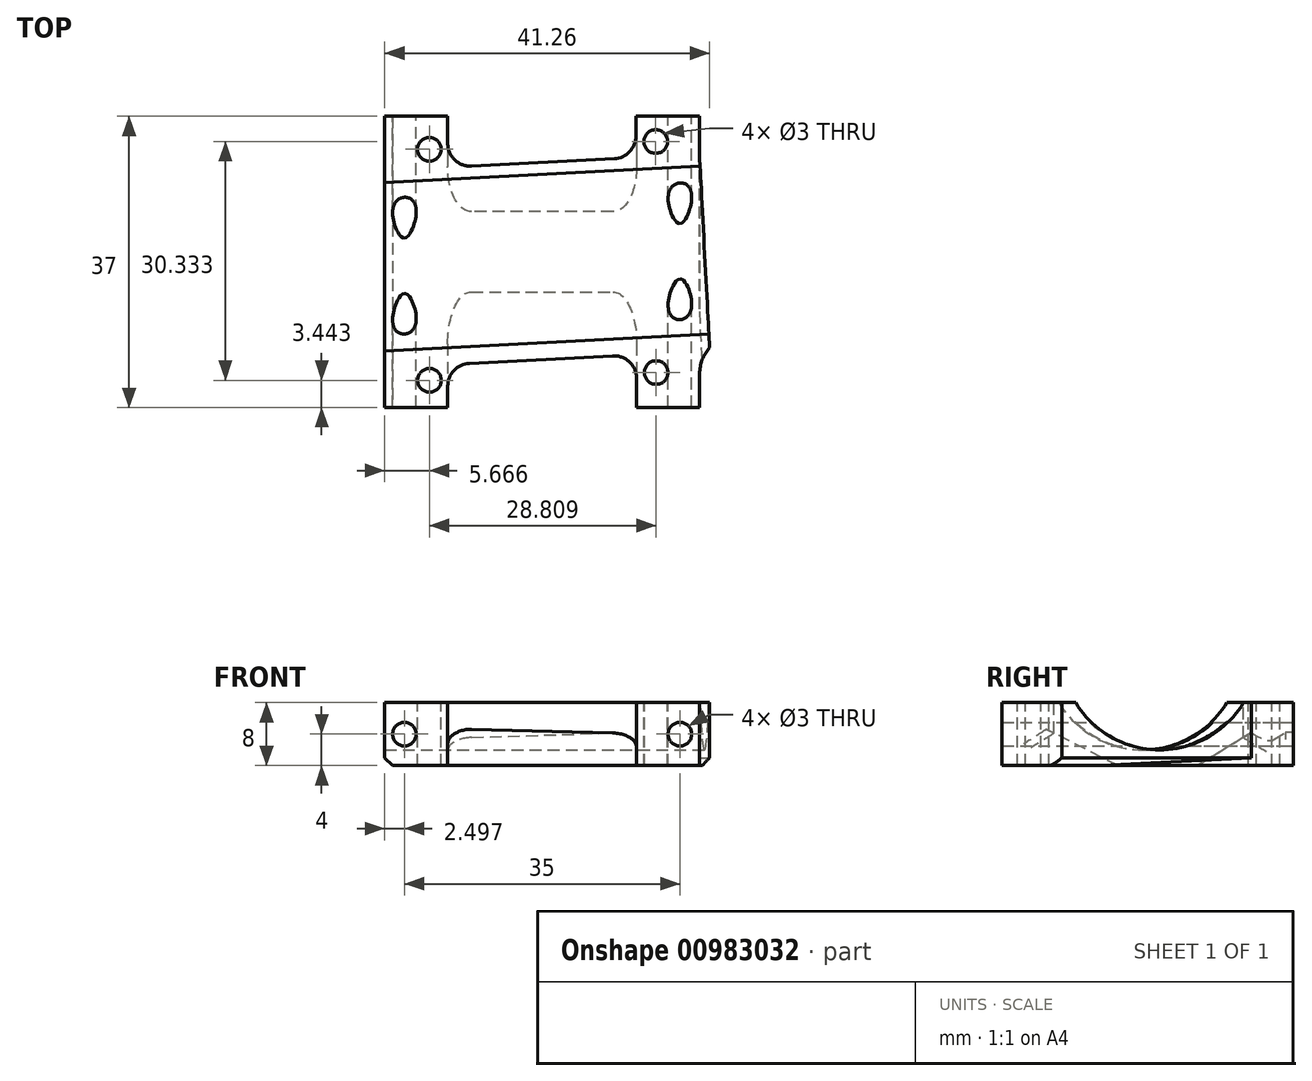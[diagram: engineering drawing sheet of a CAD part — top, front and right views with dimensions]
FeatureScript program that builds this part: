
annotation { "Feature Type Name" : "Feature", "Feature Type Description" : "" }
export const myFeature = defineFeature(function(context is Context, id is Id, definition is map)
    precondition{}
    {
        {
            var Q0;
            Q0=qCreatedBy(makeId("Top.planeOp"),FACE);
            var sketch = newSketch(context, id + "F0", { "sketchPlane" : qUnion([Q0])});
            skLineSegment(sketch, "E0.bottom", {"start": v(-25.77, 33.29) * mm, "end": v(14.23, 33.29) * mm});
            skLineSegment(sketch, "E0.top", {"start": v(-25.77, -1.71) * mm, "end": v(14.23, -1.71) * mm});
            skLineSegment(sketch, "E0.left", {"start": v(-25.77, 33.29) * mm, "end": v(-25.77, -1.71) * mm});
            skLineSegment(sketch, "E0.right", {"start": v(14.23, 33.29) * mm, "end": v(14.23, -1.71) * mm});
            skSolve(sketch);
        }
        {
            var Q0;
            Q0=qSketchRegion(id+"F0",true);
            extrude(context, id + "F1", {"entities" : qUnion([Q0]), "depth" : 8 * mm, "offsetDistance" : 25 * mm});
        }
        {
            var Q0;
            Q0=makeQuery(id+"F1.opExtrude","CAP_FACE",FACE,{"disambiguationData":[OSD([sQuery(id+"F0.wireOp",EDGE,"E0.bottom"),sQuery(id+"F0.wireOp",EDGE,"E0.top"),sQuery(id+"F0.wireOp",EDGE,"E0.left"),sQuery(id+"F0.wireOp",EDGE,"E0.right")])],"isStart":false});
            var sketch = newSketch(context, id + "F2", { "sketchPlane" : qUnion([Q0])});
            skLineSegment(sketch, "E1", {"start": v(-25.77, 28.93) * mm, "end": v(-27.03, 4.89) * mm});
            skLineSegment(sketch, "E2", {"start": v(-27.03, 4.89) * mm, "end": v(-25.77, 4.82) * mm});
            skLineSegment(sketch, "E3", {"start": v(-25.77, 4.82) * mm, "end": v(-23.4, 26.1) * mm});
            skLineSegment(sketch, "E4", {"start": v(-23.4, 26.1) * mm, "end": v(-25.77, 28.93) * mm});
            skSolve(sketch);
        }
        {
            var Q0;
            Q0=qSketchRegion(id+"F2",true);
            extrude(context, id + "F3", {"entities" : qUnion([Q0]), "operationType" : NewBodyOperationType.ADD, "oppositeDirection" : true, "depth" : 8 * mm, "offsetDistance" : 25 * mm});
        }
        {
            var Q0;
            Q0=makeQuery(id+"F3.opExtrude","SWEPT_FACE",FACE,{"disambiguationData":[OSD([sQuery(id+"F2.wireOp",EDGE,"E1")])]});
            var sketch = newSketch(context, id + "F4", { "sketchPlane" : qUnion([Q0])});
            skCircle(sketch, "E5", {"center": v(-15.9, 14.5) * mm, "radius": 12.5 * mm});
            skSolve(sketch);
        }
        {
            var Q0;
            Q0=qSketchRegion(id+"F4",true);
            extrude(context, id + "F5", {"entities" : qUnion([Q0]), "operationType" : NewBodyOperationType.REMOVE, "oppositeDirection" : true, "depth" : 64.1 * mm, "offsetDistance" : 25 * mm});
        }
        {
            var Q0;
            {var subQ1=sQuery(id+"F0.wireOp",EDGE,"E0.left");var subQ2=sQuery(id+"F0.wireOp",EDGE,"E0.right");var subQ3=sQuery(id+"F0.wireOp",EDGE,"E0.bottom");Q0=makeQuery(id+"F5.boolean.opBoolean","SPLIT",FACE,{"disambiguationData":[TD([makeQuery(id+"F1.opExtrude","SWEPT_FACE",FACE,{"disambiguationData":[OSD([subQ3])]})])],"derivedFrom":makeQuery(id+"F3.boolean.opBoolean","MERGE",FACE,{"derivedFrom":[makeQuery(id+"F1.opExtrude","CAP_FACE",FACE,{"disambiguationData":[OSD([subQ3,sQuery(id+"F0.wireOp",EDGE,"E0.top"),subQ1,subQ2])],"isStart":false}),makeQuery(id+"F3.opExtrude","CAP_FACE",FACE,{"disambiguationData":[OSD([sQuery(id+"F2.wireOp",EDGE,"E1"),sQuery(id+"F2.wireOp",EDGE,"E2"),sQuery(id+"F2.wireOp",EDGE,"E3"),sQuery(id+"F2.wireOp",EDGE,"E4")])],"isStart":true})]})});}
            var sketch = newSketch(context, id + "F6", { "sketchPlane" : qUnion([Q0])});
            skLineSegment(sketch, "E6", {"start": v(-14.93, 28.9) * mm, "end": v(3.18, 27.94) * mm});
            skLineSegment(sketch, "E7.0", {"start": v(-14.72, 3.85) * mm, "end": v(3.48, 2.9) * mm});
            skLineSegment(sketch, "E8.0", {"start": v(6.23, 0) * mm, "end": v(6.23, -1.71) * mm});
            skLineSegment(sketch, "E9.0", {"start": v(-17.77, 0.95) * mm, "end": v(-17.77, -1.71) * mm});
            skLineSegment(sketch, "E10.0", {"start": v(6.23, 33.29) * mm, "end": v(6.23, 30.84) * mm});
            skCircle(sketch, "E11", {"center": v(-20.25, 1.73) * mm, "radius": 1.5 * mm});
            skCircle(sketch, "E12", {"center": v(8.56, 30.09) * mm, "radius": 1.5 * mm});
            skCircle(sketch, "E13", {"center": v(-20.2, 31.07) * mm, "radius": 1.5 * mm});
            skLineSegment(sketch, "E14", {"start": v(-17.68, 31.79) * mm, "end": v(-17.68, 33.29) * mm});
            skPoint(sketch, "E15.visualSharp", {"position": v(-17.68, 29.04) * mm});
            skArc(sketch, "E15.filletArc", {"start": v(-17.68, 31.79) * mm, "mid": v(-16.88, 29.8) * mm, "end": v(-14.93, 28.9) * mm});
            skPoint(sketch, "E16.visualSharp", {"position": v(6.23, 27.78) * mm});
            skArc(sketch, "E16.filletArc", {"start": v(3.18, 27.94) * mm, "mid": v(5.32, 28.74) * mm, "end": v(6.23, 30.84) * mm});
            skPoint(sketch, "E17.visualSharp", {"position": v(6.23, 2.75) * mm});
            skArc(sketch, "E17.filletArc", {"start": v(6.23, 0) * mm, "mid": v(5.43, 2) * mm, "end": v(3.48, 2.9) * mm});
            skPoint(sketch, "E18.visualSharp", {"position": v(-17.77, 4) * mm});
            skArc(sketch, "E18.filletArc", {"start": v(-14.72, 3.85) * mm, "mid": v(-16.87, 3.05) * mm, "end": v(-17.77, 0.95) * mm});
            skLineSegment(sketch, "E19", {"start": v(-17.77, -1.71) * mm, "end": v(-10.84, -6.86) * mm});
            skLineSegment(sketch, "E20", {"start": v(-10.84, -6.86) * mm, "end": v(6.23, -1.71) * mm});
            skLineSegment(sketch, "E21", {"start": v(-17.68, 33.29) * mm, "end": v(-3.16, 37.2) * mm});
            skLineSegment(sketch, "E22", {"start": v(-3.16, 37.2) * mm, "end": v(6.23, 33.29) * mm});
            skCircle(sketch, "E23", {"center": v(8.55, 0.73) * mm, "radius": 1.5 * mm});
            skSolve(sketch);
        }
        {
            var Q0;
            Q0=qSketchRegion(id+"F6",true);
            extrude(context, id + "F7", {"entities" : qUnion([Q0]), "operationType" : NewBodyOperationType.REMOVE, "oppositeDirection" : true, "depth" : 25 * mm, "offsetDistance" : 25 * mm});
        }
        {
            var Q0;
            {var subQ5=sQuery(id+"F0.wireOp",EDGE,"E0.left");var subQ7=sQuery(id+"F0.wireOp",EDGE,"E0.bottom");Q0=makeQuery(id+"F7.boolean.opBoolean","SPLIT",FACE,{"disambiguationData":[TD([makeQuery(id+"F1.opExtrude","SWEPT_FACE",FACE,{"disambiguationData":[OSD([subQ5])]})])],"derivedFrom":makeQuery(id+"F1.opExtrude","SWEPT_FACE",FACE,{"disambiguationData":[OSD([subQ7])]})});}
            var sketch = newSketch(context, id + "F8", { "sketchPlane" : qUnion([Q0])});
            skCircle(sketch, "E24", {"center": v(-11.73, 4) * mm, "radius": 1.5 * mm});
            skCircle(sketch, "E25", {"center": v(23.27, 4) * mm, "radius": 1.5 * mm});
            skSolve(sketch);
        }
        {
            var Q0;
            Q0=qSketchRegion(id+"F8",true);
            extrude(context, id + "F9", {"entities" : qUnion([Q0]), "operationType" : NewBodyOperationType.REMOVE, "oppositeDirection" : true, "depth" : 46.6 * mm, "offsetDistance" : 25 * mm});
        }
        {
            var Q0;
            Q0=makeQuery(id+"F3.opExtrude","SWEPT_EDGE",EDGE,{"disambiguationData":[OSD([sQuery(id+"F0.wireOp",EDGE,"E0.left"),sQuery(id+"F2.wireOp",EDGE,"E2"),sQuery(id+"F2.wireOp",EDGE,"E3")])]});
            fillet(context, id + "F10", {"entities" : qUnion([Q0]), "radius" : 5 * mm, "tangentPropagation" : true, "allowEdgeOverflow" : false});
        }
        {
            var Q0;
            Q0=makeQuery(id+"F7.boolean.opBoolean","COPY",FACE,{"derivedFrom":makeQuery(id+"F7.opExtrude","SWEPT_FACE",FACE,{"disambiguationData":[OSD([sQuery(id+"F6.wireOp",EDGE,"E8.0")])]})});
            var sketch = newSketch(context, id + "F11", { "sketchPlane" : qUnion([Q0])});
            skLineSegment(sketch, "E26", {"start": v(-37.97, 9.77) * mm, "end": v(-21.04, -0.7) * mm});
            skLineSegment(sketch, "E27", {"start": v(-13.35, -0.7) * mm, "end": v(0, 6.1) * mm});
            skLineSegment(sketch, "E28", {"start": v(-37.97, 9.77) * mm, "end": v(-37.97, -11.82) * mm});
            skLineSegment(sketch, "E29", {"start": v(-37.97, -11.82) * mm, "end": v(-21.04, -0.7) * mm});
            skLineSegment(sketch, "E30", {"start": v(-13.35, -0.7) * mm, "end": v(-2.57, -3.45) * mm});
            skLineSegment(sketch, "E31", {"start": v(0, 6.1) * mm, "end": v(4.72, 8.5) * mm});
            skLineSegment(sketch, "E32", {"start": v(4.72, 8.5) * mm, "end": v(6.07, -10.58) * mm});
            skLineSegment(sketch, "E33", {"start": v(6.07, -10.58) * mm, "end": v(-2.57, -3.45) * mm});
            skSolve(sketch);
        }
        {
            var Q0;
            Q0=qSketchRegion(id+"F11",true);
            var Q1;
            Q1=makeQuery(id+"F7.boolean.opBoolean","COPY",FACE,{"derivedFrom":makeQuery(id+"F7.opExtrude","SWEPT_FACE",FACE,{"disambiguationData":[OSD([sQuery(id+"F6.wireOp",EDGE,"E9.0")])]})});
            extrude(context, id + "F12", {"entities" : qUnion([Q0]), "operationType" : NewBodyOperationType.REMOVE, "endBound" : BoundingType.UP_TO_SURFACE, "depth" : 25 * mm, "endBoundEntityFace" : qUnion([Q1]), "offsetDistance" : 25 * mm});
        }
        {
            var Q0;
            Q0=makeQuery(id+"F12.boolean.opBoolean","COPY",EDGE,{"derivedFrom":makeQuery(id+"F12.opExtrude","CAP_EDGE",EDGE,{"disambiguationData":[OSD([sQuery(id+"F11.wireOp",EDGE,"E26")])],"isStart":true})});
            var Q1;
            Q1=makeQuery(id+"F12.boolean.opBoolean","COPY",EDGE,{"derivedFrom":makeQuery(id+"F12.opExtrude","CAP_EDGE",EDGE,{"disambiguationData":[OSD([sQuery(id+"F11.wireOp",EDGE,"E27")])],"isStart":false})});
            var Q2;
            Q2=makeQuery(id+"F12.boolean.opBoolean","COPY",EDGE,{"derivedFrom":makeQuery(id+"F12.opExtrude","CAP_EDGE",EDGE,{"disambiguationData":[OSD([sQuery(id+"F11.wireOp",EDGE,"E26")])],"isStart":false})});
            var Q3;
            Q3=makeQuery(id+"F12.boolean.opBoolean","COPY",EDGE,{"derivedFrom":makeQuery(id+"F12.opExtrude","CAP_EDGE",EDGE,{"disambiguationData":[OSD([sQuery(id+"F11.wireOp",EDGE,"E27")])],"isStart":true})});
            fillet(context, id + "F13", {"entities" : qUnion([Q0, Q1, Q2, Q3]), "radius" : 3 * mm, "tangentPropagation" : true, "allowEdgeOverflow" : false});
        }
        {
            var Q0;
            Q0=makeQuery(id+"F1.opExtrude","CAP_EDGE",EDGE,{"disambiguationData":[OSD([sQuery(id+"F0.wireOp",EDGE,"E0.right")])],"isStart":true});
            var Q1;
            Q1=makeQuery(id+"F3.opExtrude","CAP_EDGE",EDGE,{"disambiguationData":[OSD([sQuery(id+"F2.wireOp",EDGE,"E1")])],"isStart":false});
            chamfer(context, id + "F14", {"entities" : qUnion([Q0, Q1]), "width" : 1 * mm, "tangentPropagation" : true});
        }
        {
            var Q0;
            {var subQ4=sQuery(id+"F0.wireOp",EDGE,"E0.right");var subQ6=sQuery(id+"F0.wireOp",EDGE,"E0.top");Q0=makeQuery(id+"F7.boolean.opBoolean","SPLIT",FACE,{"disambiguationData":[TD([makeQuery(id+"F1.opExtrude","SWEPT_FACE",FACE,{"disambiguationData":[OSD([subQ4])]})])],"derivedFrom":makeQuery(id+"F1.opExtrude","SWEPT_FACE",FACE,{"disambiguationData":[OSD([subQ6])]})});}
            var Q1;
            {var subQ5=sQuery(id+"F0.wireOp",EDGE,"E0.left");var subQ6=sQuery(id+"F0.wireOp",EDGE,"E0.top");Q1=makeQuery(id+"F7.boolean.opBoolean","SPLIT",FACE,{"disambiguationData":[TD([makeQuery(id+"F1.opExtrude","SWEPT_FACE",FACE,{"disambiguationData":[OSD([subQ5])]})])],"derivedFrom":makeQuery(id+"F1.opExtrude","SWEPT_FACE",FACE,{"disambiguationData":[OSD([subQ6])]})});}
            extrude(context, id + "F15", {"entities" : qUnion([Q0, Q1]), "operationType" : NewBodyOperationType.ADD, "depth" : 1 * mm, "offsetDistance" : 25 * mm});
        }
        {
            var Q0;
            {var subQ4=sQuery(id+"F0.wireOp",EDGE,"E0.right");var subQ7=sQuery(id+"F0.wireOp",EDGE,"E0.bottom");Q0=makeQuery(id+"F7.boolean.opBoolean","SPLIT",FACE,{"disambiguationData":[TD([makeQuery(id+"F1.opExtrude","SWEPT_FACE",FACE,{"disambiguationData":[OSD([subQ4])]})])],"derivedFrom":makeQuery(id+"F1.opExtrude","SWEPT_FACE",FACE,{"disambiguationData":[OSD([subQ7])]})});}
            var Q1;
            {var subQ5=sQuery(id+"F0.wireOp",EDGE,"E0.left");var subQ7=sQuery(id+"F0.wireOp",EDGE,"E0.bottom");Q1=makeQuery(id+"F7.boolean.opBoolean","SPLIT",FACE,{"disambiguationData":[TD([makeQuery(id+"F1.opExtrude","SWEPT_FACE",FACE,{"disambiguationData":[OSD([subQ5])]})])],"derivedFrom":makeQuery(id+"F1.opExtrude","SWEPT_FACE",FACE,{"disambiguationData":[OSD([subQ7])]})});}
            extrude(context, id + "F16", {"entities" : qUnion([Q0, Q1]), "operationType" : NewBodyOperationType.ADD, "depth" : 1 * mm, "offsetDistance" : 25 * mm});
        }
        {
            var Q0;
            Q0=makeQuery(id+"F1.opExtrude","SWEPT_BODY",BODY,{"disambiguationData":[OSD([sQuery(id+"F0.wireOp",EDGE,"E0.bottom"),sQuery(id+"F0.wireOp",EDGE,"E0.top"),sQuery(id+"F0.wireOp",EDGE,"E0.left"),sQuery(id+"F0.wireOp",EDGE,"E0.right")])]});
            var Q1;
            {var subQ0=sQuery(id+"F0.wireOp",EDGE,"E0.right");var subQ1=sQuery(id+"F0.wireOp",EDGE,"E0.bottom");var subQ2=sQuery(id+"F0.wireOp",EDGE,"E0.top");Q1=makeQuery(id+"F16.boolean.opBoolean","MERGE",FACE,{"derivedFrom":[makeQuery(id+"F15.boolean.opBoolean","MERGE",FACE,{"derivedFrom":[makeQuery(id+"F1.opExtrude","SWEPT_FACE",FACE,{"disambiguationData":[OSD([subQ0])]}),makeQuery(id+"F15.opExtrude","SWEPT_FACE",FACE,{"disambiguationData":[OSD([subQ2,subQ0]),TDD([makeQuery(id+"F1.opExtrude","SWEPT_EDGE",EDGE,{"disambiguationData":[OSD([subQ2,subQ0])]})])]})]}),makeQuery(id+"F16.opExtrude","SWEPT_FACE",FACE,{"disambiguationData":[OSD([subQ1,subQ0]),TDD([makeQuery(id+"F1.opExtrude","SWEPT_EDGE",EDGE,{"disambiguationData":[OSD([subQ1,subQ0])]})])]})]});}
            mirror(context, id + "F17", {"operationType" : NewBodyOperationType.ADD, "entities" : qUnion([Q0]), "mirrorPlane" : qUnion([Q1])});
        }
        {
            var Q0;
            {var subQ0=sQuery(id+"F2.wireOp",EDGE,"E1");var subQ1=makeQuery(id+"F3.opExtrude","CAP_FACE",FACE,{"disambiguationData":[OSD([subQ0,sQuery(id+"F2.wireOp",EDGE,"E2"),sQuery(id+"F2.wireOp",EDGE,"E3"),sQuery(id+"F2.wireOp",EDGE,"E4")])],"isStart":true});var subQ2=sQuery(id+"F0.wireOp",EDGE,"E0.right");var subQ3=sQuery(id+"F0.wireOp",EDGE,"E0.left");var subQ4=sQuery(id+"F0.wireOp",EDGE,"E0.bottom");var subQ5=makeQuery(id+"F1.opExtrude","CAP_FACE",FACE,{"disambiguationData":[OSD([subQ4,sQuery(id+"F0.wireOp",EDGE,"E0.top"),subQ3,subQ2])],"isStart":false});var subQ6=makeQuery(id+"F1.opExtrude","SWEPT_FACE",FACE,{"disambiguationData":[OSD([subQ2])]});var subQ7=makeQuery(id+"F1.opExtrude","SWEPT_FACE",FACE,{"disambiguationData":[OSD([subQ4])]});var subQ8=makeQuery(id+"F1.opExtrude","CAP_EDGE",EDGE,{"disambiguationData":[OSD([subQ4])],"isStart":false});var subQ9=makeQuery(id+"F1.opExtrude","SWEPT_FACE",FACE,{"disambiguationData":[OSD([subQ3])]});var subQ10=makeQuery(id+"F16.boolean.opBoolean","MERGE",FACE,{"derivedFrom":[makeQuery(id+"F5.boolean.opBoolean","SPLIT",FACE,{"disambiguationData":[TD([subQ7])],"derivedFrom":makeQuery(id+"F3.boolean.opBoolean","MERGE",FACE,{"derivedFrom":[subQ5,subQ1]})}),makeQuery(id+"F16.opExtrude","SWEPT_FACE",FACE,{"disambiguationData":[OSD([subQ4]),TDD([makeQuery(id+"F7.boolean.opBoolean","SPLIT",EDGE,{"disambiguationData":[TD([subQ9])],"derivedFrom":subQ8})])]}),makeQuery(id+"F16.opExtrude","SWEPT_FACE",FACE,{"disambiguationData":[OSD([subQ4]),TDD([makeQuery(id+"F7.boolean.opBoolean","SPLIT",EDGE,{"disambiguationData":[TD([subQ6])],"derivedFrom":subQ8})])]})]});Q0=makeQuery(id+"F17.boolean.opBoolean","MERGE",FACE,{"derivedFrom":[subQ10,makeQuery(id+"F17.opPattern","COPY",FACE,{"derivedFrom":subQ10,"instanceName":"1"})]});}
            var sketch = newSketch(context, id + "F18", { "sketchPlane" : qUnion([Q0])});
            skLineSegment(sketch, "E34.bottom", {"start": v(14.23, 34.29) * mm, "end": v(-43.35, 34.29) * mm});
            skLineSegment(sketch, "E34.top", {"start": v(14.23, -17.39) * mm, "end": v(-43.35, -17.39) * mm});
            skLineSegment(sketch, "E34.left", {"start": v(14.23, 34.29) * mm, "end": v(14.23, -17.39) * mm});
            skLineSegment(sketch, "E34.right", {"start": v(-43.35, 34.29) * mm, "end": v(-43.35, -17.39) * mm});
            skSolve(sketch);
        }
        {
            var Q0;
            Q0 = qSketchRegion(id + "F18", true);
            extrude(context, id + "F19", {"entities" : qUnion([Q0]), "operationType" : NewBodyOperationType.REMOVE, "oppositeDirection" : true, "depth" : 25 * mm, "offsetDistance" : 25 * mm});
        }
    });
